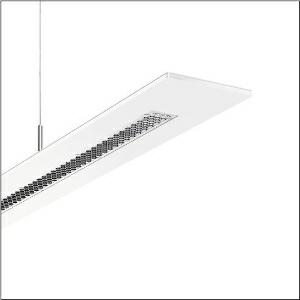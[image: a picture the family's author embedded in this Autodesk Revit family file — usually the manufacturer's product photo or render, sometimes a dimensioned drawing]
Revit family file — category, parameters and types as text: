
# Revit family: arktika_r__21_5mb251dl30830_c5c6
name_source: partatom
category: Lighting Fixtures
units: mm (PartAtom-declared; Revit-internal decimal feet)

## family parameters
Cut with Voids When Loaded = No
Host = Face
Light Source = No
Part Type = Normal
Room Calculation Point = No
Round Connector Dimension = Use Diameter
Shared = No

## types (1)
- --- (1 x LED 3000K / CRI = 80 (unbekannt), 4050 lm, 3000K)
    Apparent Load = 34 VA
    CIE Flux Codes = 81 100 100 79 100
    Color Rendering = 80
    Color Temperature = 3000K
    Default Elevation = 1800 mm
    Description = Arktika® 21, office luminaire, primary anti-glare with honeycomb louvre, of plastic, aluminium vaporised, highly specular, light emission: direct/indirect distribution, primary light characteristic: symmetric, installation type: suspended mounting, LED, rated luminous flux: 4.050lm, luminous efficacy: 120lm/W, light colour: 830, colour temperature: 3000K, control gear: DALI, with terminal, 3+2-pole, max. 2.5mm², mains connection: 220..240V, AC, 50/60Hz, rated input power: 34W, housing, of aluminium, powder-coated, traffic white (RAL 9016), 1-length, length: 1.250mm, width: 120mm, height: 8mm, protection rating (complete): IP20, insulation class (complete): insulation class II (safety insulation), certification: CE, ENEC, VDE, packaging unit: 1 piece
    Height = 8 mm  [stored 0.0262467 ft]
    Lamp = 1 x LED 3000K / CRI >= 80 (unbekannt)
    Lamp Light Flux = 4050 lm
    Lamp count = 1
    Length = 1250 mm
    Luminous efficacy = 120 lm/W
    Manufacturer = Siteco
    ModVariant = No
    Model = 5MB251DL30830
    Mounting Place = Ceiling
    Mounting Type = Pendant
    Number of Poles = 1
    OnlyDefault = Yes
    Power Factor = 1
    Product Name = Arktika® 21
    Product group = office luminaire | ceiling pendant
    ProductGroupID = 904
    Protection Class = Protection class II
    Protection Degree = IP 20
    RLX_Detail_Level = 1
    RLX_Emergency_Light_Flux = 0 lm
    RLX_Emergency_Type = 0
    RLX_Emergency_Type_DB = No
    RlxData = <blob elided: 39285 chars, md5=97d73d35>
    Socket = socket
    Standby Power = 0 W
    System Light Flux = 4050 lm
    System Power = 34 W
    Type Comments = factory setting: luminous flux: 100 % | dim-lin: 254 | 665 mA
    Type Image = l_1006128.jpg
    URL = http://relux.com
    VarID = @adj_202996
    Voltage = 0 V
    Weight = 0.00 kg
    Width = 120 mm

note: [stored X ft] marks values corroborated as IEEE doubles in the binary element streams (Revit-internal decimal feet)

## geometry (parser evidence)
native form markers: Blend x4, Sweep x13
no freeform markers — native parametric forms only
